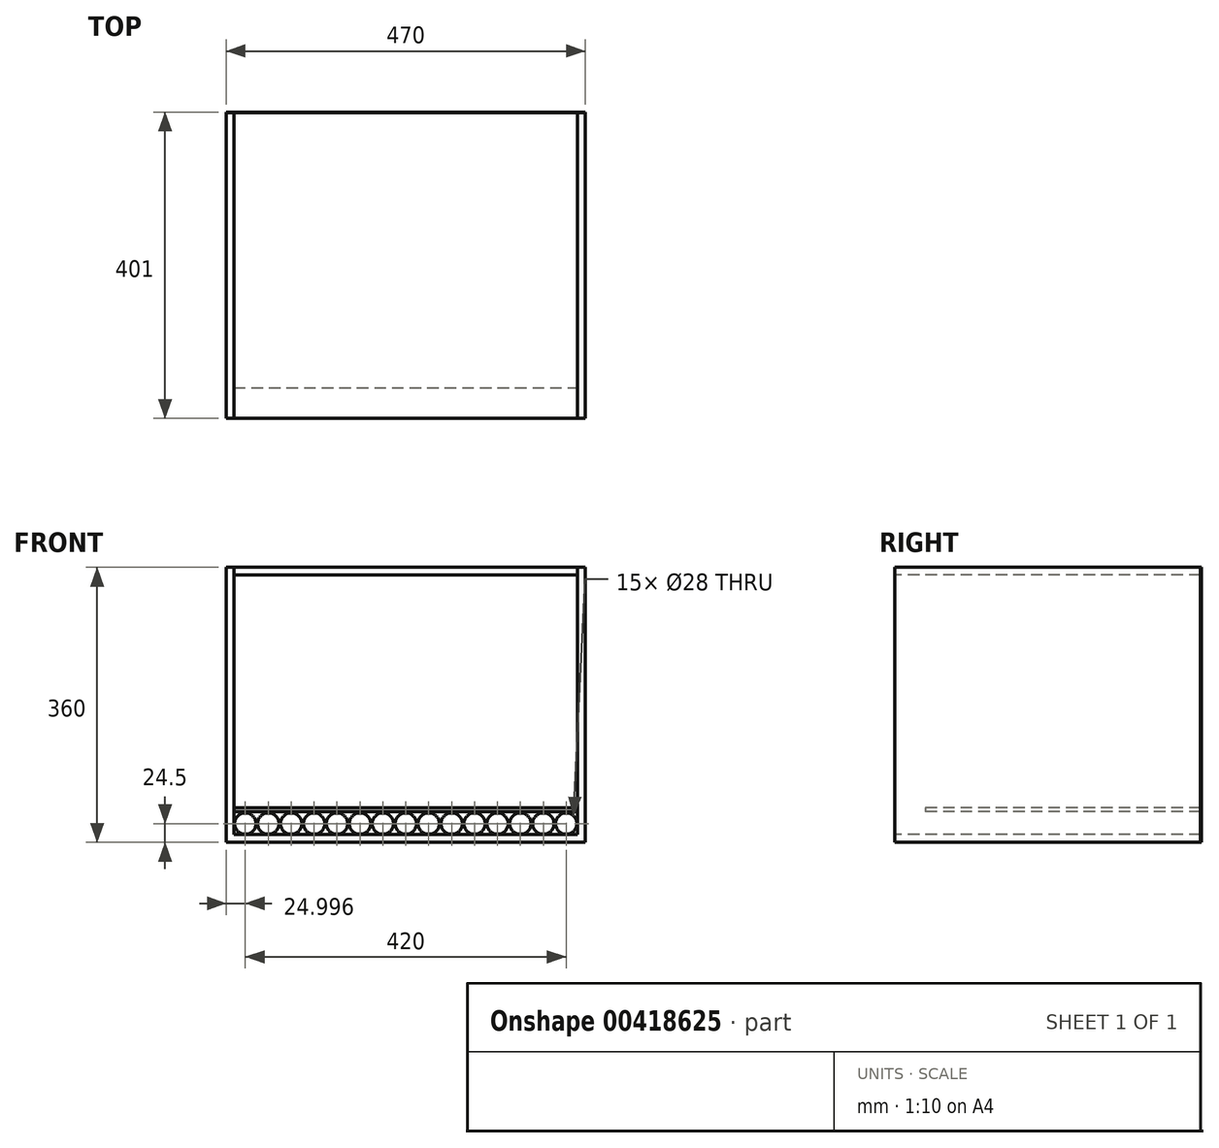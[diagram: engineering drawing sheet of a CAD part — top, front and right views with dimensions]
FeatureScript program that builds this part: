
annotation { "Feature Type Name" : "Feature", "Feature Type Description" : "" }
export const myFeature = defineFeature(function(context is Context, id is Id, definition is map)
    precondition{}
    {
        {
            var Q0;
            Q0=qCreatedBy(makeId("Top.planeOp"),FACE);
            var sketch = newSketch(context, id + "F0", { "sketchPlane" : qUnion([Q0])});
            skLineSegment(sketch, "E0.bottom", {"start": v(203.77, 198.23) * mm, "end": v(-246.23, 198.23) * mm});
            skLineSegment(sketch, "E0.top", {"start": v(203.77, -201.77) * mm, "end": v(-246.23, -201.77) * mm});
            skLineSegment(sketch, "E0.left", {"start": v(203.77, 198.23) * mm, "end": v(203.77, -201.77) * mm});
            skLineSegment(sketch, "E0.right", {"start": v(-246.23, 198.23) * mm, "end": v(-246.23, -201.77) * mm});
            skSolve(sketch);
        }
        {
            var Q0;
            Q0 = qSketchRegion(id + "F0", true);
            extrude(context, id + "F1", {"entities" : qUnion([Q0]), "depth" : 10 * mm});
        }
        {
            var Q0;
            Q0=makeQuery(id+"F1.opExtrude","SWEPT_FACE",FACE,{"disambiguationData":[OSD([sQuery(id+"F0.wireOp",EDGE,"E0.right")])]});
            cPlane(context, id + "F2", {"entities" : qUnion([Q0]), "cplaneType" : CPlaneType.OFFSET, "offset" : 0 * mm, "width" : 150 * mm, "height" : 150 * mm});
        }
        {
            var Q0;
            Q0=makeQuery(id+"F1.opExtrude","SWEPT_FACE",FACE,{"disambiguationData":[OSD([sQuery(id+"F0.wireOp",EDGE,"E0.left")])]});
            cPlane(context, id + "F3", {"entities" : qUnion([Q0]), "cplaneType" : CPlaneType.OFFSET, "offset" : 0 * mm, "width" : 150 * mm, "height" : 150 * mm});
        }
        {
            var Q0;
            Q0=makeQuery(id+"F1.opExtrude","SWEPT_FACE",FACE,{"disambiguationData":[OSD([sQuery(id+"F0.wireOp",EDGE,"E0.bottom")])]});
            cPlane(context, id + "F4", {"entities" : qUnion([Q0]), "cplaneType" : CPlaneType.OFFSET, "offset" : 0 * mm, "width" : 150 * mm, "height" : 150 * mm});
        }
        {
            var Q0;
            Q0=qCreatedBy(id+"F2.planeOp",FACE);
            var sketch = newSketch(context, id + "F5", { "sketchPlane" : qUnion([Q0])});
            skLineSegment(sketch, "E1.bottom", {"start": v(-179.33, 0) * mm, "end": v(161.01, 0) * mm});
            skLineSegment(sketch, "E1.top", {"start": v(-179.33, 72.77) * mm, "end": v(161.01, 72.77) * mm});
            skLineSegment(sketch, "E1.left", {"start": v(-179.33, 0) * mm, "end": v(-179.33, 72.77) * mm});
            skLineSegment(sketch, "E1.right", {"start": v(161.01, 0) * mm, "end": v(161.01, 72.77) * mm});
            skSolve(sketch);
        }
        {
            var Q0;
            Q0=makeQuery(id+"F5.imprint","IMPRINT",FACE,{"disambiguationData":[TD([[makeQuery(id+"F5.imprint","IMPRINT",EDGE,{"derivedFrom":sQuery(id+"F5.wireOp",EDGE,"E1.bottom")}),1.0]])]});
            extrude(context, id + "F6", {"entities" : qUnion([Q0]), "operationType" : NewBodyOperationType.ADD, "depth" : 10 * mm});
        }
        {
            var Q0;
            Q0=qCreatedBy(id+"F2.planeOp",FACE);
            var sketch = newSketch(context, id + "F7", { "sketchPlane" : qUnion([Q0])});
            skLineSegment(sketch, "E2.bottom", {"start": v(-198.23, 0) * mm, "end": v(201.77, 0) * mm});
            skLineSegment(sketch, "E2.top", {"start": v(-198.23, 360) * mm, "end": v(201.77, 360) * mm});
            skLineSegment(sketch, "E2.left", {"start": v(-198.23, 0) * mm, "end": v(-198.23, 360) * mm});
            skLineSegment(sketch, "E2.right", {"start": v(201.77, 0) * mm, "end": v(201.77, 360) * mm});
            skSolve(sketch);
        }
        {
            var Q0;
            Q0=makeQuery(id+"F7.imprint","IMPRINT",FACE,{"disambiguationData":[TD([[makeQuery(id+"F7.imprint","IMPRINT",EDGE,{"derivedFrom":sQuery(id+"F7.wireOp",EDGE,"E2.bottom")}),1.0]])]});
            extrude(context, id + "F8", {"entities" : qUnion([Q0]), "operationType" : NewBodyOperationType.ADD, "depth" : 10 * mm});
        }
        {
            var Q0;
            Q0=qCreatedBy(id+"F3.planeOp",FACE);
            var sketch = newSketch(context, id + "F9", { "sketchPlane" : qUnion([Q0])});
            skLineSegment(sketch, "E3.bottom", {"start": v(-201.77, 0) * mm, "end": v(198.23, 0) * mm});
            skLineSegment(sketch, "E3.top", {"start": v(-201.77, 360) * mm, "end": v(198.23, 360) * mm});
            skLineSegment(sketch, "E3.left", {"start": v(-201.77, 0) * mm, "end": v(-201.77, 360) * mm});
            skLineSegment(sketch, "E3.right", {"start": v(198.23, 0) * mm, "end": v(198.23, 360) * mm});
            skSolve(sketch);
        }
        {
            var Q0;
            Q0=makeQuery(id+"F9.imprint","IMPRINT",FACE,{"disambiguationData":[TD([[makeQuery(id+"F9.imprint","IMPRINT",EDGE,{"derivedFrom":sQuery(id+"F9.wireOp",EDGE,"E3.bottom")}),1.0]])]});
            extrude(context, id + "F10", {"entities" : qUnion([Q0]), "operationType" : NewBodyOperationType.ADD, "depth" : 10 * mm});
        }
        {
            var Q0;
            Q0=makeQuery(id+"F8.opExtrude","SWEPT_FACE",FACE,{"disambiguationData":[OSD([sQuery(id+"F7.wireOp",EDGE,"E2.top")])]});
            cPlane(context, id + "F11", {"entities" : qUnion([Q0]), "cplaneType" : CPlaneType.OFFSET, "offset" : 0 * mm, "width" : 150 * mm, "height" : 150 * mm});
        }
        {
            var Q0;
            Q0=qCreatedBy(id+"F11.planeOp",FACE);
            var sketch = newSketch(context, id + "F12", { "sketchPlane" : qUnion([Q0])});
            skLineSegment(sketch, "E4.bottom", {"start": v(-246.23, 198.23) * mm, "end": v(203.77, 198.23) * mm});
            skLineSegment(sketch, "E4.top", {"start": v(-246.23, -201.77) * mm, "end": v(203.77, -201.77) * mm});
            skLineSegment(sketch, "E4.left", {"start": v(-246.23, 198.23) * mm, "end": v(-246.23, -201.77) * mm});
            skLineSegment(sketch, "E4.right", {"start": v(203.77, 198.23) * mm, "end": v(203.77, -201.77) * mm});
            skSolve(sketch);
        }
        {
            var Q0;
            Q0=makeQuery(id+"F12.imprint","IMPRINT",FACE,{"disambiguationData":[TD([[makeQuery(id+"F12.imprint","IMPRINT",EDGE,{"derivedFrom":sQuery(id+"F12.wireOp",EDGE,"E4.bottom")}),-1.0]])]});
            extrude(context, id + "F13", {"entities" : qUnion([Q0]), "oppositeDirection" : true, "depth" : 10 * mm});
        }
        {
            var Q0;
            Q0=qCreatedBy(id+"F4.planeOp",FACE);
            var sketch = newSketch(context, id + "F14", { "sketchPlane" : qUnion([Q0])});
            skLineSegment(sketch, "E5.bottom", {"start": v(-213.77, 0) * mm, "end": v(256.23, 0) * mm});
            skLineSegment(sketch, "E5.top", {"start": v(-213.77, 360) * mm, "end": v(256.23, 360) * mm});
            skLineSegment(sketch, "E5.left", {"start": v(-213.77, 0) * mm, "end": v(-213.77, 360) * mm});
            skLineSegment(sketch, "E5.right", {"start": v(256.23, 0) * mm, "end": v(256.23, 360) * mm});
            skSolve(sketch);
        }
        {
            var Q0;
            Q0=makeQuery(id+"F14.imprint","IMPRINT",FACE,{"disambiguationData":[TD([[makeQuery(id+"F14.imprint","IMPRINT",EDGE,{"derivedFrom":sQuery(id+"F14.wireOp",EDGE,"E5.bottom")}),1.0]])]});
            extrude(context, id + "F15", {"entities" : qUnion([Q0]), "depth" : 1 * mm});
        }
        {
            var Q0;
            Q0=qCreatedBy(makeId("Top.planeOp"),FACE);
            cPlane(context, id + "F16", {"entities" : qUnion([Q0]), "cplaneType" : CPlaneType.OFFSET, "offset" : 40 * mm, "width" : 150 * mm, "height" : 150 * mm});
        }
        {
            var Q0;
            Q0=qCreatedBy(id+"F16.planeOp",FACE);
            var sketch = newSketch(context, id + "F17", { "sketchPlane" : qUnion([Q0])});
            skLineSegment(sketch, "E6.bottom", {"start": v(-246.23, 198.23) * mm, "end": v(203.77, 198.23) * mm});
            skLineSegment(sketch, "E6.top", {"start": v(-246.23, -161.77) * mm, "end": v(203.77, -161.77) * mm});
            skLineSegment(sketch, "E6.left", {"start": v(-246.23, 198.23) * mm, "end": v(-246.23, -161.77) * mm});
            skLineSegment(sketch, "E6.right", {"start": v(203.77, 198.23) * mm, "end": v(203.77, -161.77) * mm});
            skSolve(sketch);
        }
        {
            var Q0;
            Q0 = qSketchRegion(id + "F17", true);
            extrude(context, id + "F18", {"entities" : qUnion([Q0]), "depth" : 5 * mm});
        }
        {
            var Q0;
            Q0=makeQuery(id+"F15.opExtrude","CAP_FACE",FACE,{"disambiguationData":[OSD([sQuery(id+"F14.wireOp",EDGE,"E5.bottom"),sQuery(id+"F14.wireOp",EDGE,"E5.top"),sQuery(id+"F14.wireOp",EDGE,"E5.left"),sQuery(id+"F14.wireOp",EDGE,"E5.right")])],"isStart":false});
            var sketch = newSketch(context, id + "F19", { "sketchPlane" : qUnion([Q0])});
            skPoint(sketch, "E7", {"position": v(-188.77, 24.5) * mm});
            skPoint(sketch, "E8", {"position": v(-158.77, 24.5) * mm});
            skPoint(sketch, "E9", {"position": v(-128.77, 24.5) * mm});
            skPoint(sketch, "E10", {"position": v(-96.8, 24.68) * mm});
            skPoint(sketch, "E11", {"position": v(-62.34, 25.63) * mm});
            skPoint(sketch, "E12", {"position": v(-10.36, 25.63) * mm});
            skPoint(sketch, "E13", {"position": v(-107.35, 24.5) * mm});
            skPoint(sketch, "E14", {"position": v(-76.8, 24.5) * mm});
            skPoint(sketch, "E15", {"position": v(-38.77, 24.5) * mm});
            skPoint(sketch, "E16", {"position": v(-8.77, 24.5) * mm});
            skPoint(sketch, "E17", {"position": v(81.23, 24.5) * mm});
            skPoint(sketch, "E18", {"position": v(111.23, 24.5) * mm});
            skPoint(sketch, "E19", {"position": v(141.23, 24.5) * mm});
            skPoint(sketch, "E20", {"position": v(171.23, 24.5) * mm});
            skPoint(sketch, "E21", {"position": v(201.23, 24.5) * mm});
            skPoint(sketch, "E22", {"position": v(231.23, 24.5) * mm});
            skPoint(sketch, "E23", {"position": v(51.23, 24.5) * mm});
            skPoint(sketch, "E24", {"position": v(21.23, 24.5) * mm});
            skPoint(sketch, "E25", {"position": v(-68.77, 24.5) * mm});
            skPoint(sketch, "E26", {"position": v(-98.77, 24.5) * mm});
            skSolve(sketch);
        }
        {
            var Q0;
            Q0=sQuery(id+"F19.wireOp",VERTEX,"E7");
            var Q1;
            Q1=sQuery(id+"F19.wireOp",VERTEX,"E8");
            var Q2;
            Q2=sQuery(id+"F19.wireOp",VERTEX,"E9");
            var Q3;
            Q3=sQuery(id+"F19.wireOp",VERTEX,"E26");
            var Q4;
            Q4=sQuery(id+"F19.wireOp",VERTEX,"E25");
            var Q5;
            Q5=sQuery(id+"F19.wireOp",VERTEX,"E15");
            var Q6;
            Q6=sQuery(id+"F19.wireOp",VERTEX,"E16");
            var Q7;
            Q7=sQuery(id+"F19.wireOp",VERTEX,"E24");
            var Q8;
            Q8=sQuery(id+"F19.wireOp",VERTEX,"E23");
            var Q9;
            Q9=sQuery(id+"F19.wireOp",VERTEX,"E17");
            var Q10;
            Q10=sQuery(id+"F19.wireOp",VERTEX,"E18");
            var Q11;
            Q11=sQuery(id+"F19.wireOp",VERTEX,"E19");
            var Q12;
            Q12=sQuery(id+"F19.wireOp",VERTEX,"E20");
            var Q13;
            Q13=sQuery(id+"F19.wireOp",VERTEX,"E21");
            var Q14;
            Q14=sQuery(id+"F19.wireOp",VERTEX,"E22");
            var Q15;
            Q15=makeQuery(id+"F15.opExtrude","SWEPT_BODY",BODY,{"disambiguationData":[OSD([sQuery(id+"F14.wireOp",EDGE,"E5.bottom"),sQuery(id+"F14.wireOp",EDGE,"E5.top"),sQuery(id+"F14.wireOp",EDGE,"E5.left"),sQuery(id+"F14.wireOp",EDGE,"E5.right")])]});
            hole(context, id + "F20", {"style" : HoleStyle.SIMPLE, "endStyle" : HoleEndStyle.THROUGH, "holeDiameter" : 28 * mm, "isTappedThrough" : true, "tappedDepth" : 12 * mm, "tapClearance" : 3, "locations" : qUnion([Q0, Q1, Q2, Q3, Q4, Q5, Q6, Q7, Q8, Q9, Q10, Q11, Q12, Q13, Q14]), "scope" : qUnion([Q15])});
        }
    });
